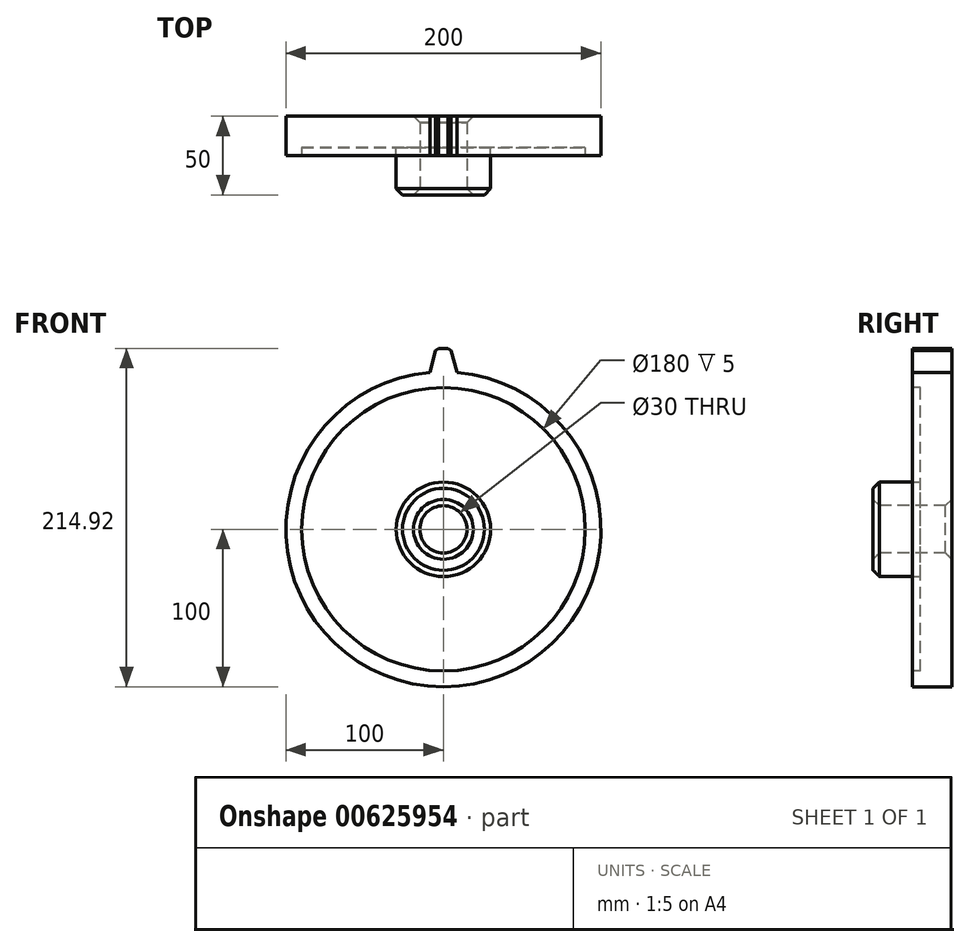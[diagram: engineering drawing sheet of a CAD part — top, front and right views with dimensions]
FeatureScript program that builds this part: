
annotation { "Feature Type Name" : "Feature", "Feature Type Description" : "" }
export const myFeature = defineFeature(function(context is Context, id is Id, definition is map)
    precondition{}
    {
        {
            var Q0;
            Q0=qCreatedBy(makeId("Front.planeOp"),FACE);
            var sketch = newSketch(context, id + "F0", { "sketchPlane" : qUnion([Q0])});
            skCircle(sketch, "E0", {"center": v(0, 0) * mm, "radius": 100 * mm});
            skSolve(sketch);
        }
        {
            var Q0;
            Q0 = qSketchRegion(id + "F0", true);
            extrude(context, id + "F1", {"entities" : qUnion([Q0]), "depth" : 25 * mm, "offsetDistance" : 25 * mm});
        }
        {
            var Q0;
            Q0=qCreatedBy(makeId("Front.planeOp"),FACE);
            var sketch = newSketch(context, id + "F2", { "sketchPlane" : qUnion([Q0])});
            skLineSegment(sketch, "E1", {"start": v(-8.6, 99.63) * mm, "end": v(8.6, 99.63) * mm});
            skLineSegment(sketch, "E2", {"start": v(8.6, 99.63) * mm, "end": v(4.5, 114.92) * mm});
            skLineSegment(sketch, "E3", {"start": v(4.5, 114.92) * mm, "end": v(-4.5, 114.92) * mm});
            skLineSegment(sketch, "E4", {"start": v(-4.5, 114.92) * mm, "end": v(-8.6, 99.63) * mm});
            skSolve(sketch);
        }
        {
            var Q0;
            Q0=makeQuery(id+"F2.imprint","IMPRINT",FACE,{"disambiguationData":[TD([[makeQuery(id+"F2.imprint","IMPRINT",EDGE,{"derivedFrom":sQuery(id+"F2.wireOp",EDGE,"E1")}),1.0]])]});
            extrude(context, id + "F3", {"entities" : qUnion([Q0]), "operationType" : NewBodyOperationType.ADD, "depth" : 25 * mm, "offsetDistance" : 25 * mm});
        }
        {
            var Q0;
            Q0=makeQuery(id+"F3.opExtrude","SWEPT_EDGE",EDGE,{"disambiguationData":[OSD([sQuery(id+"F2.wireOp",EDGE,"E2"),sQuery(id+"F2.wireOp",EDGE,"E3")])]});
            var Q1;
            Q1=makeQuery(id+"F3.opExtrude","SWEPT_EDGE",EDGE,{"disambiguationData":[OSD([sQuery(id+"F2.wireOp",EDGE,"E3"),sQuery(id+"F2.wireOp",EDGE,"E4")])]});
            chamfer(context, id + "F4", {"entities" : qUnion([Q0, Q1]), "width" : 2 * mm, "tangentPropagation" : true});
        }
        {
            var Q0;
            Q0=makeQuery(id+"F3.opExtrude","SWEPT_EDGE",EDGE,{"disambiguationData":[OSD([sQuery(id+"F2.wireOp",EDGE,"E1"),sQuery(id+"F2.wireOp",EDGE,"E2")])]});
            var Q1;
            Q1=makeQuery(id+"F3.opExtrude","SWEPT_EDGE",EDGE,{"disambiguationData":[OSD([sQuery(id+"F2.wireOp",EDGE,"E1"),sQuery(id+"F2.wireOp",EDGE,"E4")])]});
            fillet(context, id + "F5", {"entities" : qUnion([Q0, Q1]), "radius" : 5 * mm, "tangentPropagation" : true, "allowEdgeOverflow" : false});
        }
        {
            var Q0;
            {var subQ0=sQuery(id+"F2.wireOp",EDGE,"E4");var subQ1=sQuery(id+"F2.wireOp",EDGE,"E3");var subQ2=sQuery(id+"F2.wireOp",EDGE,"E2");var subQ3=sQuery(id+"F2.wireOp",EDGE,"E1");Q0=makeQuery(id+"FUCCzStfiEJRbJ8_1.19.F3.boolean.opBoolean","MERGE",FACE,{"derivedFrom":[makeQuery(id+"FUCCzStfiEJRbJ8_1.18.F3.boolean.opBoolean","MERGE",FACE,{"derivedFrom":[makeQuery(id+"FUCCzStfiEJRbJ8_1.17.F3.boolean.opBoolean","MERGE",FACE,{"derivedFrom":[makeQuery(id+"FUCCzStfiEJRbJ8_1.16.F3.boolean.opBoolean","MERGE",FACE,{"derivedFrom":[makeQuery(id+"FUCCzStfiEJRbJ8_1.15.F3.boolean.opBoolean","MERGE",FACE,{"derivedFrom":[makeQuery(id+"FUCCzStfiEJRbJ8_1.14.F3.boolean.opBoolean","MERGE",FACE,{"derivedFrom":[makeQuery(id+"FUCCzStfiEJRbJ8_1.13.F3.boolean.opBoolean","MERGE",FACE,{"derivedFrom":[makeQuery(id+"FUCCzStfiEJRbJ8_1.12.F3.boolean.opBoolean","MERGE",FACE,{"derivedFrom":[makeQuery(id+"FUCCzStfiEJRbJ8_1.11.F3.boolean.opBoolean","MERGE",FACE,{"derivedFrom":[makeQuery(id+"FUCCzStfiEJRbJ8_1.10.F3.boolean.opBoolean","MERGE",FACE,{"derivedFrom":[makeQuery(id+"FUCCzStfiEJRbJ8_1.9.F3.boolean.opBoolean","MERGE",FACE,{"derivedFrom":[makeQuery(id+"FUCCzStfiEJRbJ8_1.8.F3.boolean.opBoolean","MERGE",FACE,{"derivedFrom":[makeQuery(id+"FUCCzStfiEJRbJ8_1.7.F3.boolean.opBoolean","MERGE",FACE,{"derivedFrom":[makeQuery(id+"FUCCzStfiEJRbJ8_1.6.F3.boolean.opBoolean","MERGE",FACE,{"derivedFrom":[makeQuery(id+"FUCCzStfiEJRbJ8_1.5.F3.boolean.opBoolean","MERGE",FACE,{"derivedFrom":[makeQuery(id+"FUCCzStfiEJRbJ8_1.4.F3.boolean.opBoolean","MERGE",FACE,{"derivedFrom":[makeQuery(id+"FUCCzStfiEJRbJ8_1.3.F3.boolean.opBoolean","MERGE",FACE,{"derivedFrom":[makeQuery(id+"FUCCzStfiEJRbJ8_1.2.F3.boolean.opBoolean","MERGE",FACE,{"derivedFrom":[makeQuery(id+"FUCCzStfiEJRbJ8_1.1.F3.boolean.opBoolean","MERGE",FACE,{"derivedFrom":[makeQuery(id+"F3.boolean.opBoolean","MERGE",FACE,{"derivedFrom":[makeQuery(id+"F1.opExtrude","CAP_FACE",FACE,{"disambiguationData":[OSD([sQuery(id+"F0.wireOp",EDGE,"E0")])],"isStart":false}),makeQuery(id+"F3.opExtrude","CAP_FACE",FACE,{"disambiguationData":[OSD([subQ3,subQ2,subQ1,subQ0])],"isStart":false})]}),makeQuery(id+"FUCCzStfiEJRbJ8_1.1.F3.opExtrude","CAP_FACE",FACE,{"disambiguationData":[OSD([subQ3,subQ2,subQ1,subQ0])],"isStart":false})]}),makeQuery(id+"FUCCzStfiEJRbJ8_1.2.F3.opExtrude","CAP_FACE",FACE,{"disambiguationData":[OSD([subQ3,subQ2,subQ1,subQ0])],"isStart":false})]}),makeQuery(id+"FUCCzStfiEJRbJ8_1.3.F3.opExtrude","CAP_FACE",FACE,{"disambiguationData":[OSD([subQ3,subQ2,subQ1,subQ0])],"isStart":false})]}),makeQuery(id+"FUCCzStfiEJRbJ8_1.4.F3.opExtrude","CAP_FACE",FACE,{"disambiguationData":[OSD([subQ3,subQ2,subQ1,subQ0])],"isStart":false})]}),makeQuery(id+"FUCCzStfiEJRbJ8_1.5.F3.opExtrude","CAP_FACE",FACE,{"disambiguationData":[OSD([subQ3,subQ2,subQ1,subQ0])],"isStart":false})]}),makeQuery(id+"FUCCzStfiEJRbJ8_1.6.F3.opExtrude","CAP_FACE",FACE,{"disambiguationData":[OSD([subQ3,subQ2,subQ1,subQ0])],"isStart":false})]}),makeQuery(id+"FUCCzStfiEJRbJ8_1.7.F3.opExtrude","CAP_FACE",FACE,{"disambiguationData":[OSD([subQ3,subQ2,subQ1,subQ0])],"isStart":false})]}),makeQuery(id+"FUCCzStfiEJRbJ8_1.8.F3.opExtrude","CAP_FACE",FACE,{"disambiguationData":[OSD([subQ3,subQ2,subQ1,subQ0])],"isStart":false})]}),makeQuery(id+"FUCCzStfiEJRbJ8_1.9.F3.opExtrude","CAP_FACE",FACE,{"disambiguationData":[OSD([subQ3,subQ2,subQ1,subQ0])],"isStart":false})]}),makeQuery(id+"FUCCzStfiEJRbJ8_1.10.F3.opExtrude","CAP_FACE",FACE,{"disambiguationData":[OSD([subQ3,subQ2,subQ1,subQ0])],"isStart":false})]}),makeQuery(id+"FUCCzStfiEJRbJ8_1.11.F3.opExtrude","CAP_FACE",FACE,{"disambiguationData":[OSD([subQ3,subQ2,subQ1,subQ0])],"isStart":false})]}),makeQuery(id+"FUCCzStfiEJRbJ8_1.12.F3.opExtrude","CAP_FACE",FACE,{"disambiguationData":[OSD([subQ3,subQ2,subQ1,subQ0])],"isStart":false})]}),makeQuery(id+"FUCCzStfiEJRbJ8_1.13.F3.opExtrude","CAP_FACE",FACE,{"disambiguationData":[OSD([subQ3,subQ2,subQ1,subQ0])],"isStart":false})]}),makeQuery(id+"FUCCzStfiEJRbJ8_1.14.F3.opExtrude","CAP_FACE",FACE,{"disambiguationData":[OSD([subQ3,subQ2,subQ1,subQ0])],"isStart":false})]}),makeQuery(id+"FUCCzStfiEJRbJ8_1.15.F3.opExtrude","CAP_FACE",FACE,{"disambiguationData":[OSD([subQ3,subQ2,subQ1,subQ0])],"isStart":false})]}),makeQuery(id+"FUCCzStfiEJRbJ8_1.16.F3.opExtrude","CAP_FACE",FACE,{"disambiguationData":[OSD([subQ3,subQ2,subQ1,subQ0])],"isStart":false})]}),makeQuery(id+"FUCCzStfiEJRbJ8_1.17.F3.opExtrude","CAP_FACE",FACE,{"disambiguationData":[OSD([subQ3,subQ2,subQ1,subQ0])],"isStart":false})]}),makeQuery(id+"FUCCzStfiEJRbJ8_1.18.F3.opExtrude","CAP_FACE",FACE,{"disambiguationData":[OSD([subQ3,subQ2,subQ1,subQ0])],"isStart":false})]}),makeQuery(id+"FUCCzStfiEJRbJ8_1.19.F3.opExtrude","CAP_FACE",FACE,{"disambiguationData":[OSD([subQ3,subQ2,subQ1,subQ0])],"isStart":false})]});}
            var sketch = newSketch(context, id + "F6", { "sketchPlane" : qUnion([Q0])});
            skCircle(sketch, "E5", {"center": v(0, 0) * mm, "radius": 90 * mm});
            skSolve(sketch);
        }
        {
            var Q0;
            Q0 = qSketchRegion(id + "F6", true);
            extrude(context, id + "F7", {"entities" : qUnion([Q0]), "operationType" : NewBodyOperationType.REMOVE, "oppositeDirection" : true, "depth" : 5 * mm, "offsetDistance" : 25 * mm});
        }
        {
            var Q0;
            Q0=makeQuery(id+"F7.boolean.opBoolean","COPY",FACE,{"derivedFrom":makeQuery(id+"F7.opExtrude","CAP_FACE",FACE,{"disambiguationData":[OSD([sQuery(id+"F6.wireOp",EDGE,"E5")])],"isStart":false})});
            var sketch = newSketch(context, id + "F8", { "sketchPlane" : qUnion([Q0])});
            skCircle(sketch, "E6", {"center": v(0, 0) * mm, "radius": 30 * mm});
            skSolve(sketch);
        }
        {
            var Q0;
            Q0 = qSketchRegion(id + "F8", true);
            extrude(context, id + "F9", {"entities" : qUnion([Q0]), "operationType" : NewBodyOperationType.ADD, "depth" : 30 * mm, "offsetDistance" : 25 * mm});
        }
        {
            var Q0;
            Q0=makeQuery(id+"F9.opExtrude","CAP_FACE",FACE,{"disambiguationData":[OSD([sQuery(id+"F8.wireOp",EDGE,"E6")])],"isStart":false});
            var sketch = newSketch(context, id + "F10", { "sketchPlane" : qUnion([Q0])});
            skCircle(sketch, "E7", {"center": v(0, 0) * mm, "radius": 15 * mm});
            skSolve(sketch);
        }
        {
            var Q0;
            Q0 = qSketchRegion(id + "F10", true);
            extrude(context, id + "F11", {"entities" : qUnion([Q0]), "operationType" : NewBodyOperationType.REMOVE, "endBound" : BoundingType.THROUGH_ALL, "oppositeDirection" : true, "depth" : 25 * mm, "offsetDistance" : 25 * mm});
        }
        {
            var Q0;
            Q0=makeQuery(id+"F9.opExtrude","CAP_EDGE",EDGE,{"disambiguationData":[OSD([sQuery(id+"F8.wireOp",EDGE,"E6")])],"isStart":false});
            var Q1;
            Q1=makeQuery(id+"F11.boolean.opBoolean","COPY",FACE,{"derivedFrom":makeQuery(id+"F11.opExtrude","SWEPT_FACE",FACE,{"disambiguationData":[OSD([sQuery(id+"F10.wireOp",EDGE,"E7")])]})});
            chamfer(context, id + "F12", {"entities" : qUnion([Q0, Q1]), "width" : 4 * mm, "tangentPropagation" : true});
        }
    });
